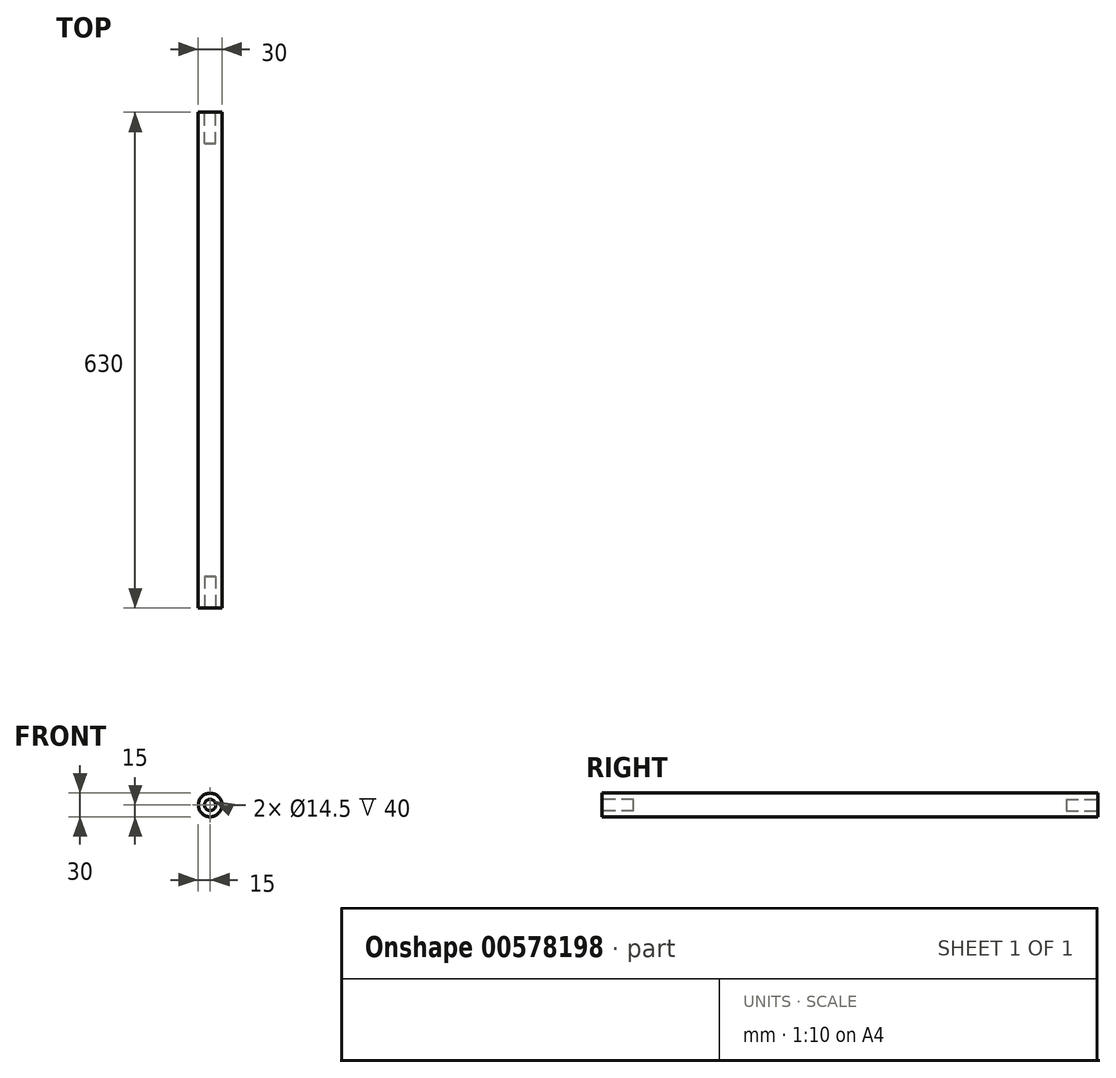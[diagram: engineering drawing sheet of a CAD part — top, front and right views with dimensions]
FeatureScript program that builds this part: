
annotation { "Feature Type Name" : "Feature", "Feature Type Description" : "" }
export const myFeature = defineFeature(function(context is Context, id is Id, definition is map)
    precondition{}
    {
        {
            var Q0;
            Q0=qCreatedBy(makeId("Front.planeOp"),FACE);
            var sketch = newSketch(context, id + "F0", { "sketchPlane" : qUnion([Q0])});
            skCircle(sketch, "E0", {"center": v(0, 0) * mm, "radius": 15 * mm});
            skSolve(sketch);
        }
        {
            var Q0;
            Q0=makeQuery(id+"F0.imprint","IMPRINT",FACE,{"disambiguationData":[TD([[makeQuery(id+"F0.imprint","IMPRINT",EDGE,{"derivedFrom":sQuery(id+"F0.wireOp",EDGE,"E0")}),1.0]])]});
            extrude(context, id + "F1", {"entities" : qUnion([Q0]), "endBound" : BoundingType.SYMMETRIC, "depth" : 630 * mm, "offsetDistance" : 25 * mm});
        }
        {
            var Q0;
            Q0=makeQuery(id+"F1.opExtrude","CAP_FACE",FACE,{"disambiguationData":[OSD([sQuery(id+"F0.wireOp",EDGE,"E0")])],"isStart":false});
            var sketch = newSketch(context, id + "F2", { "sketchPlane" : qUnion([Q0])});
            skCircle(sketch, "E1.0.0", {"center": v(0, 0) * mm, "radius": 15 * mm});
            skCircle(sketch, "E2", {"center": v(0, 0) * mm, "radius": 7.25 * mm});
            skSolve(sketch);
        }
        {
            var Q0;
            Q0=makeQuery(id+"F2.imprint","IMPRINT",FACE,{"disambiguationData":[TD([[makeQuery(id+"F2.imprint","IMPRINT",EDGE,{"derivedFrom":sQuery(id+"F2.wireOp",EDGE,"E2")}),1.0]])]});
            extrude(context, id + "F3", {"entities" : qUnion([Q0]), "operationType" : NewBodyOperationType.REMOVE, "oppositeDirection" : true, "depth" : 40 * mm, "offsetDistance" : 25 * mm});
        }
        {
            var Q0;
            Q0=makeQuery(id+"F1.opExtrude","CAP_FACE",FACE,{"disambiguationData":[OSD([sQuery(id+"F0.wireOp",EDGE,"E0")])],"isStart":true});
            var sketch = newSketch(context, id + "F4", { "sketchPlane" : qUnion([Q0])});
            skCircle(sketch, "E3.0.0", {"center": v(0, 0) * mm, "radius": 15 * mm});
            skCircle(sketch, "E4", {"center": v(0, 0) * mm, "radius": 7.25 * mm});
            skSolve(sketch);
        }
        {
            var Q0;
            Q0=makeQuery(id+"F4.imprint","IMPRINT",FACE,{"disambiguationData":[TD([[makeQuery(id+"F4.imprint","IMPRINT",EDGE,{"derivedFrom":sQuery(id+"F4.wireOp",EDGE,"E4")}),1.0]])]});
            extrude(context, id + "F5", {"entities" : qUnion([Q0]), "operationType" : NewBodyOperationType.REMOVE, "oppositeDirection" : true, "depth" : 40 * mm, "offsetDistance" : 25 * mm});
        }
    });
